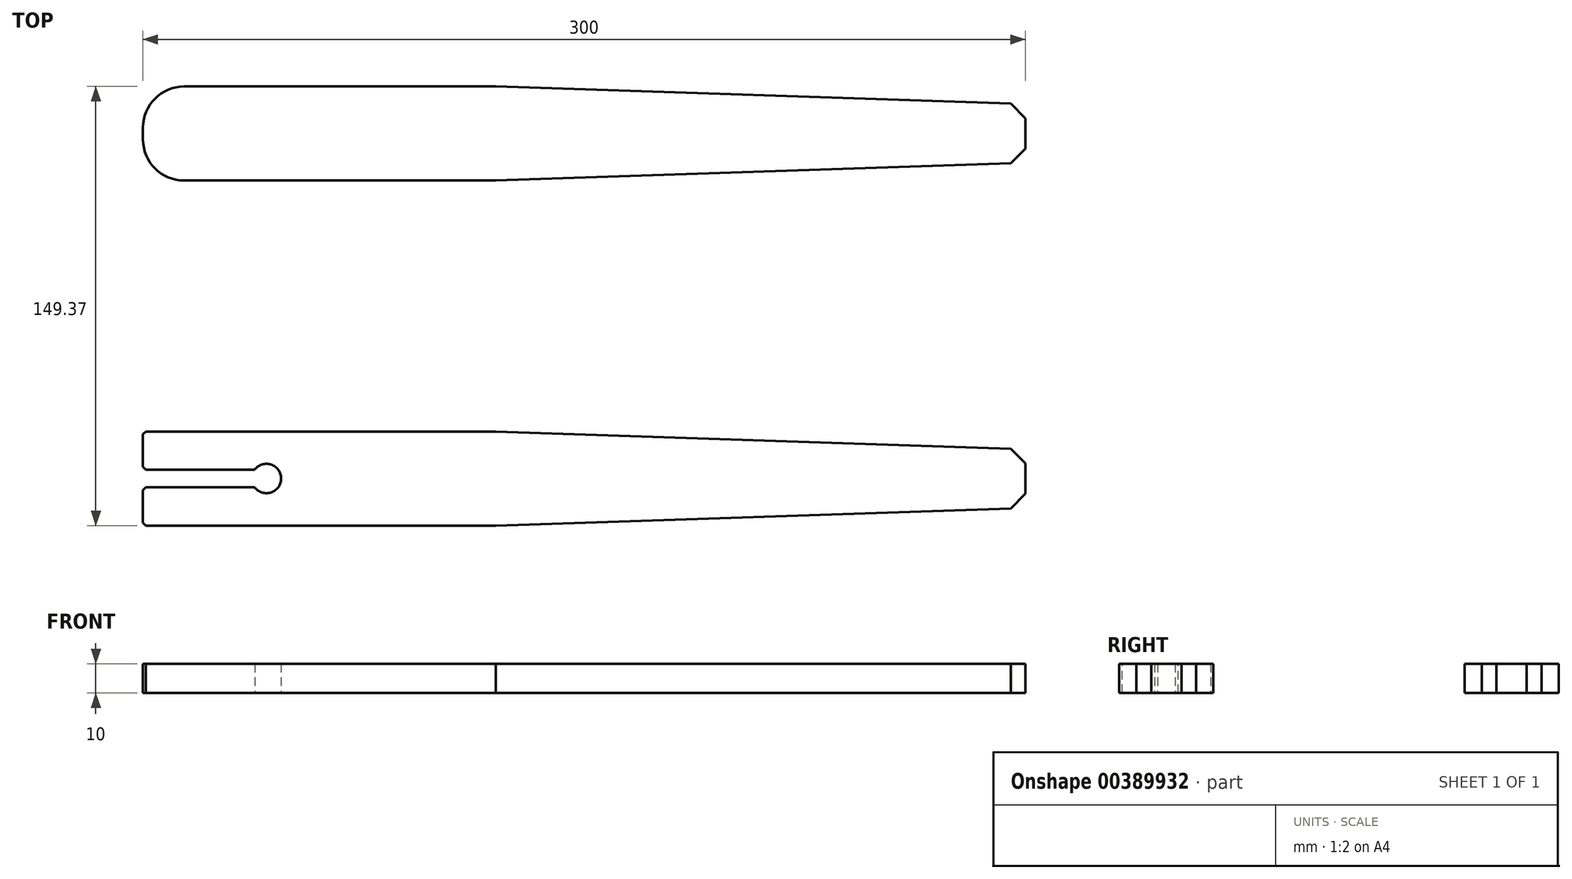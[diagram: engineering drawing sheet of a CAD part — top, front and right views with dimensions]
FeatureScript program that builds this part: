
annotation { "Feature Type Name" : "Feature", "Feature Type Description" : "" }
export const myFeature = defineFeature(function(context is Context, id is Id, definition is map)
    precondition{}
    {
        {
            var Q0;
            Q0=qCreatedBy(makeId("Top.planeOp"),FACE);
            var sketch = newSketch(context, id + "F0", { "sketchPlane" : qUnion([Q0])});
            skLineSegment(sketch, "E0", {"start": v(0, 32) * mm, "end": v(-300, 32) * mm, "construction": true});
            skLineSegment(sketch, "E1", {"start": v(0, 32) * mm, "end": v(0, 26) * mm, "construction": true});
            skLineSegment(sketch, "E2", {"start": v(0, 26) * mm, "end": v(0, 6) * mm, "construction": true});
            skLineSegment(sketch, "E3", {"start": v(0, 6) * mm, "end": v(0, 0) * mm, "construction": true});
            skLineSegment(sketch, "E4", {"start": v(0, 0) * mm, "end": v(-300, 0) * mm, "construction": true});
            skLineSegment(sketch, "E5", {"start": v(-300, 0) * mm, "end": v(-300, 32) * mm, "construction": true});
            skLineSegment(sketch, "E6", {"start": v(0, 0) * mm, "end": v(-180, 0) * mm, "construction": true});
            skLineSegment(sketch, "E7", {"start": v(-180, 32) * mm, "end": v(0, 32) * mm, "construction": true});
            skLineSegment(sketch, "E8", {"start": v(0, -85.37) * mm, "end": v(-300, -85.37) * mm, "construction": true});
            skLineSegment(sketch, "E9", {"start": v(0, -85.37) * mm, "end": v(0, -91.37) * mm, "construction": true});
            skLineSegment(sketch, "E10", {"start": v(0, -91.37) * mm, "end": v(0, -111.37) * mm, "construction": true});
            skLineSegment(sketch, "E11", {"start": v(0, -111.37) * mm, "end": v(0, -117.37) * mm, "construction": true});
            skLineSegment(sketch, "E12", {"start": v(0, -117.37) * mm, "end": v(-300, -117.37) * mm, "construction": true});
            skLineSegment(sketch, "E13", {"start": v(-300, -117.37) * mm, "end": v(-300, -85.37) * mm, "construction": true});
            skLineSegment(sketch, "E14", {"start": v(0, -117.37) * mm, "end": v(-180, -117.37) * mm, "construction": true});
            skLineSegment(sketch, "E15", {"start": v(-180, -85.37) * mm, "end": v(0, -85.37) * mm, "construction": true});
            skLineSegment(sketch, "E16", {"start": v(-300, -85.37) * mm, "end": v(-300, -101.37) * mm, "construction": true});
            skLineSegment(sketch, "E17", {"start": v(-300, -101.37) * mm, "end": v(-258, -101.37) * mm, "construction": true});
            skLineSegment(sketch, "E18", {"start": v(-300, -85.37) * mm, "end": v(-300, -98.37) * mm, "construction": true});
            skLineSegment(sketch, "E19", {"start": v(-300, -117.37) * mm, "end": v(-300, -104.37) * mm, "construction": true});
            skLineSegment(sketch, "E20", {"start": v(0, 26) * mm, "end": v(-180, 32) * mm});
            skLineSegment(sketch, "E21", {"start": v(-180, 32) * mm, "end": v(-300, 32) * mm});
            skLineSegment(sketch, "E22", {"start": v(-300, 32) * mm, "end": v(-300, 0) * mm});
            skLineSegment(sketch, "E23", {"start": v(-300, 0) * mm, "end": v(-180, 0) * mm});
            skLineSegment(sketch, "E24", {"start": v(-180, 0) * mm, "end": v(0, 6) * mm});
            skLineSegment(sketch, "E25", {"start": v(0, 6) * mm, "end": v(0, 26) * mm});
            skLineSegment(sketch, "E26", {"start": v(0, -91.37) * mm, "end": v(-180, -85.37) * mm});
            skLineSegment(sketch, "E27", {"start": v(-180, -85.37) * mm, "end": v(-300, -85.37) * mm});
            skLineSegment(sketch, "E28", {"start": v(-300, -85.37) * mm, "end": v(-300, -98.37) * mm});
            skLineSegment(sketch, "E29", {"start": v(-300, -104.37) * mm, "end": v(-300, -117.37) * mm});
            skLineSegment(sketch, "E30", {"start": v(-300, -117.37) * mm, "end": v(-180, -117.37) * mm});
            skLineSegment(sketch, "E31", {"start": v(-180, -117.37) * mm, "end": v(0, -111.37) * mm});
            skLineSegment(sketch, "E32", {"start": v(0, -111.37) * mm, "end": v(0, -91.37) * mm});
            skArc(sketch, "E33", {"start": v(-262, -104.37) * mm, "mid": v(-253, -101.37) * mm, "end": v(-262, -98.37) * mm});
            skLineSegment(sketch, "E34", {"start": v(-300, -98.37) * mm, "end": v(-262, -98.37) * mm});
            skLineSegment(sketch, "E35", {"start": v(-300, -104.37) * mm, "end": v(-262, -104.37) * mm});
            skSolve(sketch);
        }
        {
            var Q0;
            Q0=makeQuery(id+"F0.imprint","IMPRINT",FACE,{"disambiguationData":[TD([[makeQuery(id+"F0.imprint","IMPRINT",EDGE,{"derivedFrom":sQuery(id+"F0.wireOp",EDGE,"E26")}),1.0]])]});
            var Q1;
            Q1=makeQuery(id+"F0.imprint","IMPRINT",FACE,{"disambiguationData":[TD([[makeQuery(id+"F0.imprint","IMPRINT",EDGE,{"derivedFrom":sQuery(id+"F0.wireOp",EDGE,"E20")}),1.0]])]});
            extrude(context, id + "F1", {"entities" : qUnion([Q0, Q1]), "depth" : 10 * mm});
        }
        {
            var Q0;
            Q0=makeQuery(id+"F1.opExtrude","SWEPT_EDGE",EDGE,{"disambiguationData":[OSD([sQuery(id+"F0.wireOp",EDGE,"E21"),sQuery(id+"F0.wireOp",EDGE,"E22")])]});
            var Q1;
            Q1=makeQuery(id+"F1.opExtrude","SWEPT_EDGE",EDGE,{"disambiguationData":[OSD([sQuery(id+"F0.wireOp",EDGE,"E22"),sQuery(id+"F0.wireOp",EDGE,"E23")])]});
            fillet(context, id + "F2", {"entities" : qUnion([Q0, Q1]), "radius" : 14 * mm, "tangentPropagation" : true, "allowEdgeOverflow" : false});
        }
        {
            var Q0;
            Q0=makeQuery(id+"F1.opExtrude","SWEPT_EDGE",EDGE,{"disambiguationData":[OSD([sQuery(id+"F0.wireOp",EDGE,"E20"),sQuery(id+"F0.wireOp",EDGE,"E25")])]});
            var Q1;
            Q1=makeQuery(id+"F1.opExtrude","SWEPT_EDGE",EDGE,{"disambiguationData":[OSD([sQuery(id+"F0.wireOp",EDGE,"E24"),sQuery(id+"F0.wireOp",EDGE,"E25")])]});
            var Q2;
            Q2=makeQuery(id+"F1.opExtrude","SWEPT_EDGE",EDGE,{"disambiguationData":[OSD([sQuery(id+"F0.wireOp",EDGE,"E26"),sQuery(id+"F0.wireOp",EDGE,"E32")])]});
            var Q3;
            Q3=makeQuery(id+"F1.opExtrude","SWEPT_EDGE",EDGE,{"disambiguationData":[OSD([sQuery(id+"F0.wireOp",EDGE,"E31"),sQuery(id+"F0.wireOp",EDGE,"E32")])]});
            chamfer(context, id + "F3", {"entities" : qUnion([Q0, Q1, Q2, Q3]), "width" : 5 * mm, "tangentPropagation" : true});
        }
        {
            var Q0;
            Q0=makeQuery(id+"F1.opExtrude","SWEPT_EDGE",EDGE,{"disambiguationData":[OSD([sQuery(id+"F0.wireOp",EDGE,"E27"),sQuery(id+"F0.wireOp",EDGE,"E28")])]});
            var Q1;
            Q1=makeQuery(id+"F1.opExtrude","SWEPT_EDGE",EDGE,{"disambiguationData":[OSD([sQuery(id+"F0.wireOp",EDGE,"E28"),sQuery(id+"F0.wireOp",EDGE,"E34")])]});
            var Q2;
            Q2=makeQuery(id+"F1.opExtrude","SWEPT_EDGE",EDGE,{"disambiguationData":[OSD([sQuery(id+"F0.wireOp",EDGE,"E29"),sQuery(id+"F0.wireOp",EDGE,"E35")])]});
            var Q3;
            Q3=makeQuery(id+"F1.opExtrude","SWEPT_EDGE",EDGE,{"disambiguationData":[OSD([sQuery(id+"F0.wireOp",EDGE,"E29"),sQuery(id+"F0.wireOp",EDGE,"E30")])]});
            chamfer(context, id + "F4", {"entities" : qUnion([Q0, Q1, Q2, Q3]), "width" : 1 * mm, "tangentPropagation" : true});
        }
    });
